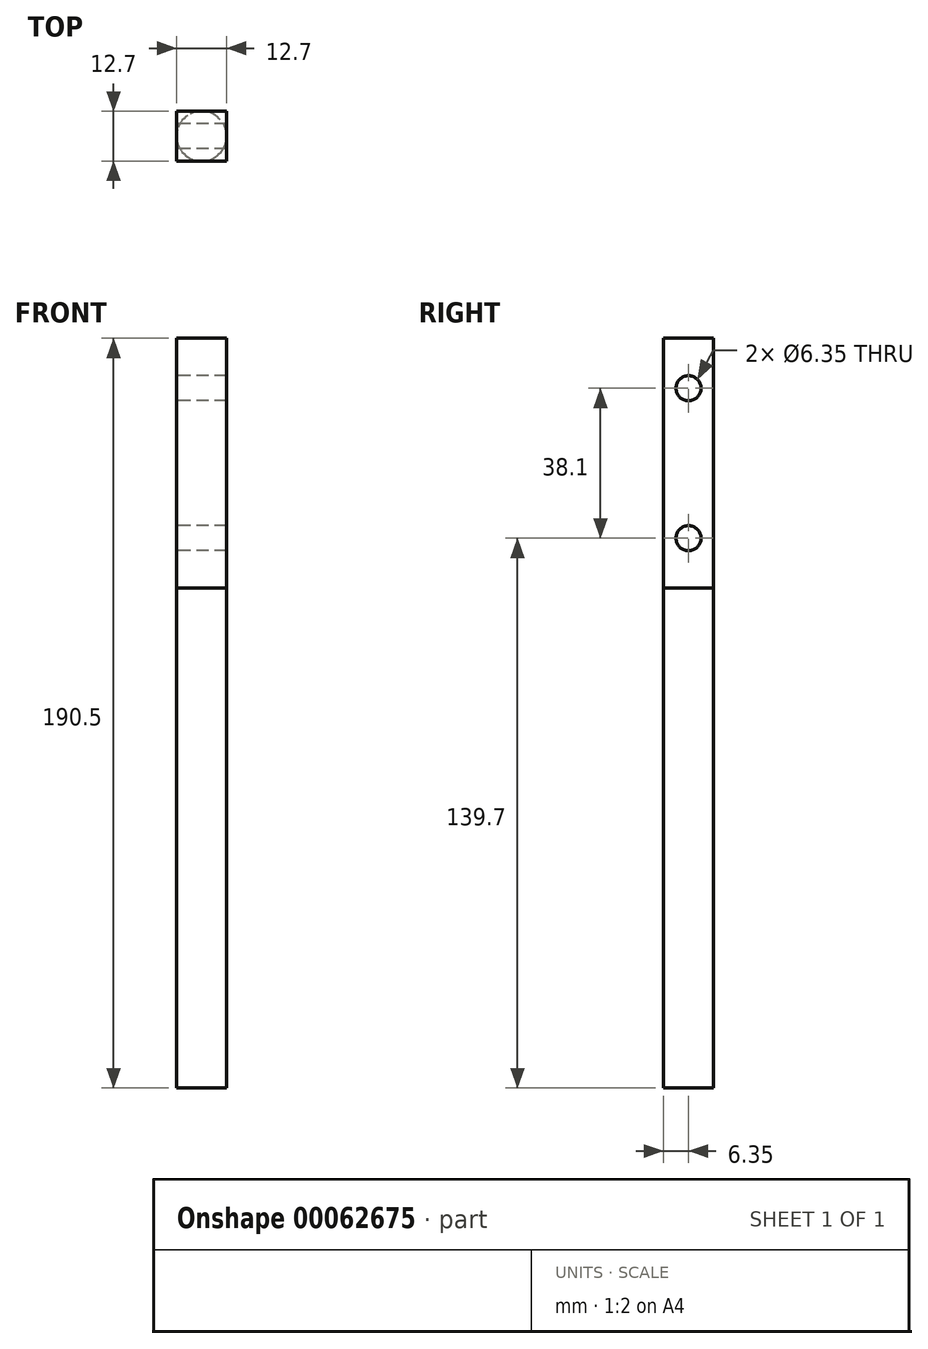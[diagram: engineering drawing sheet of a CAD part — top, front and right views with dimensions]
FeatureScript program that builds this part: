
annotation { "Feature Type Name" : "Feature", "Feature Type Description" : "" }
export const myFeature = defineFeature(function(context is Context, id is Id, definition is map)
    precondition{}
    {
        {
            var Q0;
            Q0=qCreatedBy(makeId("Top.planeOp"),FACE);
            var sketch = newSketch(context, id + "F0", { "sketchPlane" : qUnion([Q0])});
            skCircle(sketch, "E0", {"center": v(0, 0) * mm, "radius": 6.35 * mm});
            skSolve(sketch);
        }
        {
            var Q0;
            Q0=makeQuery(id+"F0.imprint","IMPRINT",FACE,{"disambiguationData":[TD([[makeQuery(id+"F0.imprint","IMPRINT",EDGE,{"derivedFrom":sQuery(id+"F0.wireOp",EDGE,"E0")}),1.0]])]});
            extrude(context, id + "F1", {"entities" : qUnion([Q0]), "depth" : 127 * mm});
        }
        {
            var Q0;
            Q0=makeQuery(id+"F1.opExtrude","CAP_FACE",FACE,{"disambiguationData":[OSD([sQuery(id+"F0.wireOp",EDGE,"E0")])],"isStart":false});
            var sketch = newSketch(context, id + "F2", { "sketchPlane" : qUnion([Q0])});
            skLineSegment(sketch, "E1.bottom", {"start": v(-6.35, 6.35) * mm, "end": v(6.35, 6.35) * mm});
            skLineSegment(sketch, "E1.top", {"start": v(-6.35, -6.35) * mm, "end": v(6.35, -6.35) * mm});
            skLineSegment(sketch, "E1.left", {"start": v(-6.35, 6.35) * mm, "end": v(-6.35, -6.35) * mm});
            skLineSegment(sketch, "E1.right", {"start": v(6.35, 6.35) * mm, "end": v(6.35, -6.35) * mm});
            skSolve(sketch);
        }
        {
            var Q0;
            {var subQ0=sQuery(id+"F2.wireOp",EDGE,"E1.left");var subQ1=sQuery(id+"F2.wireOp",EDGE,"E1.bottom");var subQ2=makeQuery(id+"F2.imprint","INTERSECT",VERTEX,{"derivedFrom":[subQ1,subQ0]});Q0=makeQuery(id+"F2.imprint","IMPRINT",FACE,{"disambiguationData":[TD([[makeQuery(id+"F2.imprint","IMPRINT",EDGE,{"disambiguationData":[TD([[subQ2,-1.0]])],"derivedFrom":subQ1}),-1.0]])]});}
            var Q1;
            {var subQ0=makeQuery(id+"F1.opExtrude","CAP_EDGE",EDGE,{"disambiguationData":[OSD([sQuery(id+"F0.wireOp",EDGE,"E0")])],"isStart":false});var subQ1=makeQuery(id+"F2.imprint","INTERSECT",VERTEX,{"derivedFrom":[subQ0,sQuery(id+"F2.wireOp",EDGE,"E1.bottom")]});Q1=makeQuery(id+"F2.imprint","IMPRINT",FACE,{"disambiguationData":[TD([[makeQuery(id+"F2.imprint","IMPRINT",EDGE,{"disambiguationData":[TD([[subQ1,-1.0]])],"derivedFrom":subQ0}),1.0]])]});}
            var Q2;
            {var subQ0=sQuery(id+"F2.wireOp",EDGE,"E1.right");var subQ1=sQuery(id+"F2.wireOp",EDGE,"E1.bottom");var subQ2=makeQuery(id+"F2.imprint","INTERSECT",VERTEX,{"derivedFrom":[subQ1,subQ0]});Q2=makeQuery(id+"F2.imprint","IMPRINT",FACE,{"disambiguationData":[TD([[makeQuery(id+"F2.imprint","IMPRINT",EDGE,{"disambiguationData":[TD([[subQ2,1.0]])],"derivedFrom":subQ1}),-1.0]])]});}
            var Q3;
            {var subQ0=sQuery(id+"F2.wireOp",EDGE,"E1.right");var subQ1=sQuery(id+"F2.wireOp",EDGE,"E1.top");var subQ2=makeQuery(id+"F2.imprint","INTERSECT",VERTEX,{"derivedFrom":[subQ1,subQ0]});Q3=makeQuery(id+"F2.imprint","IMPRINT",FACE,{"disambiguationData":[TD([[makeQuery(id+"F2.imprint","IMPRINT",EDGE,{"disambiguationData":[TD([[subQ2,1.0]])],"derivedFrom":subQ1}),1.0]])]});}
            var Q4;
            {var subQ0=sQuery(id+"F2.wireOp",EDGE,"E1.left");var subQ1=sQuery(id+"F2.wireOp",EDGE,"E1.top");var subQ2=makeQuery(id+"F2.imprint","INTERSECT",VERTEX,{"derivedFrom":[subQ1,subQ0]});Q4=makeQuery(id+"F2.imprint","IMPRINT",FACE,{"disambiguationData":[TD([[makeQuery(id+"F2.imprint","IMPRINT",EDGE,{"disambiguationData":[TD([[subQ2,-1.0]])],"derivedFrom":subQ1}),1.0]])]});}
            extrude(context, id + "F3", {"entities" : qUnion([Q0, Q1, Q2, Q3, Q4]), "operationType" : NewBodyOperationType.ADD, "depth" : 63.5 * mm});
        }
        {
            var Q0;
            Q0=makeQuery(id+"F3.opExtrude","SWEPT_FACE",FACE,{"disambiguationData":[OSD([sQuery(id+"F2.wireOp",EDGE,"E1.right")])]});
            var sketch = newSketch(context, id + "F4", { "sketchPlane" : qUnion([Q0])});
            skCircle(sketch, "E2", {"center": v(0, 177.8) * mm, "radius": 3.18 * mm});
            skCircle(sketch, "E3", {"center": v(0, 139.7) * mm, "radius": 3.18 * mm});
            skSolve(sketch);
        }
        {
            var Q0;
            Q0=sQuery(id+"F4.wireOp",VERTEX,"E2.center");
            var Q1;
            Q1=sQuery(id+"F4.wireOp",VERTEX,"E3.center");
            var Q2;
            Q2=makeQuery(id+"F1.opExtrude","SWEPT_BODY",BODY,{"disambiguationData":[OSD([sQuery(id+"F0.wireOp",EDGE,"E0")])]});
            hole(context, id + "F5", {"style" : HoleStyle.SIMPLE, "holeDiameter" : 6.35 * mm, "endStyle" : HoleEndStyle.THROUGH, "locations" : qUnion([Q0, Q1]), "scope" : qUnion([Q2])});
        }
    });
